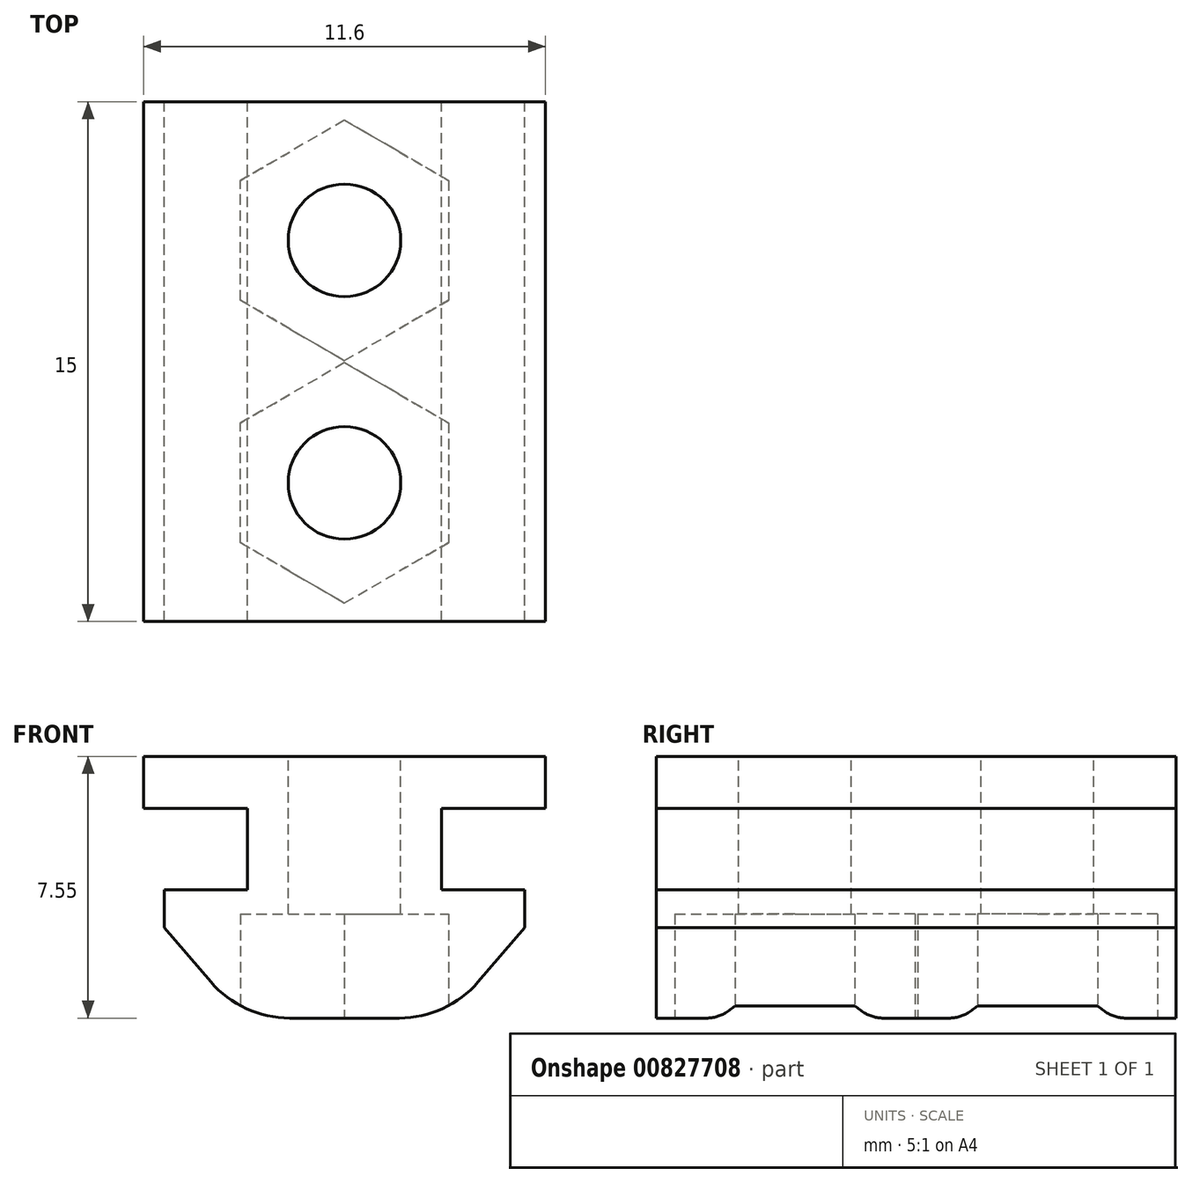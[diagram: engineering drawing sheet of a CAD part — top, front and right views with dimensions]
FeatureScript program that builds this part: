
annotation { "Feature Type Name" : "Feature", "Feature Type Description" : "" }
export const myFeature = defineFeature(function(context is Context, id is Id, definition is map)
    precondition{}
    {
        {
            var Q0;
            Q0=qCreatedBy(makeId("Front.planeOp"),FACE);
            var sketch = newSketch(context, id + "F0", { "sketchPlane" : qUnion([Q0])});
            skPoint(sketch, "E0.middle", {"position": v(0, 0) * mm});
            skLineSegment(sketch, "E1.0", {"start": v(2.8, 10) * mm, "end": v(2.8, 7.9) * mm});
            skLineSegment(sketch, "E1.1", {"start": v(2.8, 7.9) * mm, "end": v(5.2, 7.9) * mm});
            skLineSegment(sketch, "E1.2", {"start": v(5.2, 7.9) * mm, "end": v(5.2, 6.81) * mm});
            skLineSegment(sketch, "E1.3", {"start": v(5.2, 6.81) * mm, "end": v(2.96, 4.2) * mm});
            skLineSegment(sketch, "E1.4", {"start": v(2.96, 4.2) * mm, "end": v(0, 4.2) * mm});
            skLineSegment(sketch, "E1.5", {"start": v(-2.96, 4.2) * mm, "end": v(0, 4.2) * mm});
            skLineSegment(sketch, "E1.6", {"start": v(-2.8, 10) * mm, "end": v(-2.8, 7.9) * mm});
            skLineSegment(sketch, "E1.7", {"start": v(-2.8, 7.9) * mm, "end": v(-5.2, 7.9) * mm});
            skLineSegment(sketch, "E1.8", {"start": v(-5.2, 7.9) * mm, "end": v(-5.2, 6.81) * mm});
            skLineSegment(sketch, "E1.9", {"start": v(-5.2, 6.81) * mm, "end": v(-2.96, 4.2) * mm});
            skLineSegment(sketch, "E2", {"start": v(-2.8, 10) * mm, "end": v(-2.8, 10.25) * mm});
            skLineSegment(sketch, "E3", {"start": v(-2.8, 10.25) * mm, "end": v(-5.8, 10.25) * mm});
            skLineSegment(sketch, "E4", {"start": v(-5.8, 10.25) * mm, "end": v(-5.8, 11.75) * mm});
            skLineSegment(sketch, "E5", {"start": v(-5.8, 11.75) * mm, "end": v(0, 11.75) * mm});
            skLineSegment(sketch, "E6.MirrorCS", {"start": v(5.8, 11.75) * mm, "end": v(0, 11.75) * mm});
            skLineSegment(sketch, "E7.MirrorCS", {"start": v(5.8, 10.25) * mm, "end": v(5.8, 11.75) * mm});
            skLineSegment(sketch, "E8.MirrorCS", {"start": v(2.8, 10.25) * mm, "end": v(5.8, 10.25) * mm});
            skLineSegment(sketch, "E9.MirrorCS", {"start": v(2.8, 10) * mm, "end": v(2.8, 10.25) * mm});
            skSolve(sketch);
        }
        {
            var Q0;
            Q0=makeQuery(id+"F0.imprint","IMPRINT",FACE,{"disambiguationData":[TD([[makeQuery(id+"F0.imprint","IMPRINT",EDGE,{"derivedFrom":sQuery(id+"F0.wireOp",EDGE,"E1.0")}),-1.0]])]});
            extrude(context, id + "F1", {"entities" : qUnion([Q0]), "depth" : 15 * mm, "offsetDistance" : 25 * mm});
        }
        {
            var Q0;
            Q0=makeQuery(id+"F1.opExtrude","SWEPT_EDGE",EDGE,{"disambiguationData":[OSD([sQuery(id+"F0.wireOp",EDGE,"E1.5"),sQuery(id+"F0.wireOp",EDGE,"E1.9")])]});
            var Q1;
            Q1=makeQuery(id+"F1.opExtrude","SWEPT_EDGE",EDGE,{"disambiguationData":[OSD([sQuery(id+"F0.wireOp",EDGE,"E1.3"),sQuery(id+"F0.wireOp",EDGE,"E1.4")])]});
            fillet(context, id + "F2", {"entities" : qUnion([Q0, Q1]), "radius" : 3 * mm, "tangentPropagation" : true, "allowEdgeOverflow" : false});
        }
        {
            var Q0;
            Q0=makeQuery(id+"F1.opExtrude","SWEPT_FACE",FACE,{"disambiguationData":[OSD([sQuery(id+"F0.wireOp",EDGE,"E5"),sQuery(id+"F0.wireOp",EDGE,"E6.MirrorCS")])]});
            var sketch = newSketch(context, id + "F3", { "sketchPlane" : qUnion([Q0])});
            skCircle(sketch, "E10", {"center": v(0, -4) * mm, "radius": 1.63 * mm});
            skCircle(sketch, "E11", {"center": v(0, -11) * mm, "radius": 1.63 * mm});
            skSolve(sketch);
        }
        {
            var Q0;
            Q0=makeQuery(id+"F3.imprint","IMPRINT",FACE,{"disambiguationData":[TD([[makeQuery(id+"F3.imprint","IMPRINT",EDGE,{"derivedFrom":sQuery(id+"F3.wireOp",EDGE,"E10")}),1.0]])]});
            var Q1;
            Q1=makeQuery(id+"F3.imprint","IMPRINT",FACE,{"disambiguationData":[TD([[makeQuery(id+"F3.imprint","IMPRINT",EDGE,{"derivedFrom":sQuery(id+"F3.wireOp",EDGE,"E11")}),1.0]])]});
            extrude(context, id + "F4", {"entities" : qUnion([Q0, Q1]), "operationType" : NewBodyOperationType.REMOVE, "oppositeDirection" : true, "depth" : 6 * mm, "offsetDistance" : 25 * mm});
        }
        {
            var Q0;
            Q0=makeQuery(id+"F1.opExtrude","SWEPT_FACE",FACE,{"disambiguationData":[OSD([sQuery(id+"F0.wireOp",EDGE,"E1.4"),sQuery(id+"F0.wireOp",EDGE,"E1.5")])]});
            var sketch = newSketch(context, id + "F5", { "sketchPlane" : qUnion([Q0])});
            skCircle(sketch, "E12.0", {"center": v(0, 11) * mm, "radius": 1.63 * mm, "construction": true});
            skCircle(sketch, "E12.1", {"center": v(0, 4) * mm, "radius": 1.63 * mm, "construction": true});
            skLineSegment(sketch, "E13.0", {"start": v(0, 14.46) * mm, "end": v(3, 12.73) * mm});
            skLineSegment(sketch, "E13.1", {"start": v(3, 12.73) * mm, "end": v(3, 9.27) * mm});
            skLineSegment(sketch, "E13.2", {"start": v(3, 9.27) * mm, "end": v(0, 7.54) * mm});
            skLineSegment(sketch, "E13.3", {"start": v(0, 7.54) * mm, "end": v(-3, 9.27) * mm});
            skLineSegment(sketch, "E13.4", {"start": v(-3, 9.27) * mm, "end": v(-3, 12.73) * mm});
            skLineSegment(sketch, "E13.5", {"start": v(-3, 12.73) * mm, "end": v(0, 14.46) * mm});
            skPoint(sketch, "E13.0.midPoint", {"position": v(0, 14) * mm});
            skLineSegment(sketch, "E14.0", {"start": v(0, 7.46) * mm, "end": v(3, 5.73) * mm});
            skLineSegment(sketch, "E14.1", {"start": v(3, 5.73) * mm, "end": v(3, 2.27) * mm});
            skLineSegment(sketch, "E14.2", {"start": v(3, 2.27) * mm, "end": v(0, 0.54) * mm});
            skLineSegment(sketch, "E14.3", {"start": v(0, 0.54) * mm, "end": v(-3, 2.27) * mm});
            skLineSegment(sketch, "E14.4", {"start": v(-3, 2.27) * mm, "end": v(-3, 5.73) * mm});
            skLineSegment(sketch, "E14.5", {"start": v(-3, 5.73) * mm, "end": v(0, 7.46) * mm});
            skPoint(sketch, "E14.0.midPoint", {"position": v(0, 7) * mm});
            skSolve(sketch);
        }
        {
            var Q0;
            {var subQ0=sQuery(id+"F5.wireOp",EDGE,"E13.0");var subQ1=sQuery(id+"F0.wireOp",EDGE,"E1.5");var subQ2=sQuery(id+"F0.wireOp",EDGE,"E1.4");var subQ3=makeQuery(id+"F1.opExtrude","SWEPT_FACE",FACE,{"disambiguationData":[OSD([subQ2,subQ1])]});var subQ4=makeQuery(id+"F2.opFillet","BLEND_EDGE",EDGE,{"blendedFrom":[makeQuery(id+"F1.opExtrude","SWEPT_EDGE",EDGE,{"disambiguationData":[OSD([subQ1,sQuery(id+"F0.wireOp",EDGE,"E1.9")])]}),subQ3],"blendedInto":[subQ3]});var subQ5=makeQuery(id+"F5.imprint","INTERSECT",VERTEX,{"derivedFrom":[subQ4,subQ0]});Q0=makeQuery(id+"F5.imprint","IMPRINT",FACE,{"disambiguationData":[TD([[makeQuery(id+"F5.imprint","IMPRINT",EDGE,{"disambiguationData":[TD([[subQ5,-1.0]])],"derivedFrom":subQ0}),-1.0]])]});}
            var Q1;
            {var subQ5=sQuery(id+"F5.wireOp",EDGE,"E13.1");Q1=makeQuery(id+"F5.imprint","IMPRINT",FACE,{"disambiguationData":[TD([[makeQuery(id+"F5.imprint","IMPRINT",EDGE,{"derivedFrom":subQ5}),-1.0]])]});}
            var Q2;
            {var subQ1=sQuery(id+"F5.wireOp",EDGE,"E13.4");Q2=makeQuery(id+"F5.imprint","IMPRINT",FACE,{"disambiguationData":[TD([[makeQuery(id+"F5.imprint","IMPRINT",EDGE,{"derivedFrom":subQ1}),-1.0]])]});}
            var Q3;
            {var subQ0=sQuery(id+"F5.wireOp",EDGE,"E14.0");var subQ1=sQuery(id+"F0.wireOp",EDGE,"E1.5");var subQ2=sQuery(id+"F0.wireOp",EDGE,"E1.4");var subQ3=makeQuery(id+"F1.opExtrude","SWEPT_FACE",FACE,{"disambiguationData":[OSD([subQ2,subQ1])]});var subQ4=makeQuery(id+"F2.opFillet","BLEND_EDGE",EDGE,{"blendedFrom":[makeQuery(id+"F1.opExtrude","SWEPT_EDGE",EDGE,{"disambiguationData":[OSD([subQ1,sQuery(id+"F0.wireOp",EDGE,"E1.9")])]}),subQ3],"blendedInto":[subQ3]});var subQ5=makeQuery(id+"F5.imprint","INTERSECT",VERTEX,{"derivedFrom":[subQ4,subQ0]});Q3=makeQuery(id+"F5.imprint","IMPRINT",FACE,{"disambiguationData":[TD([[makeQuery(id+"F5.imprint","IMPRINT",EDGE,{"disambiguationData":[TD([[subQ5,-1.0]])],"derivedFrom":subQ0}),-1.0]])]});}
            var Q4;
            {var subQ1=sQuery(id+"F5.wireOp",EDGE,"E14.4");Q4=makeQuery(id+"F5.imprint","IMPRINT",FACE,{"disambiguationData":[TD([[makeQuery(id+"F5.imprint","IMPRINT",EDGE,{"derivedFrom":subQ1}),-1.0]])]});}
            var Q5;
            {var subQ5=sQuery(id+"F5.wireOp",EDGE,"E14.1");Q5=makeQuery(id+"F5.imprint","IMPRINT",FACE,{"disambiguationData":[TD([[makeQuery(id+"F5.imprint","IMPRINT",EDGE,{"derivedFrom":subQ5}),-1.0]])]});}
            var Q6;
            {var subQ0=sQuery(id+"F5.wireOp",EDGE,"E13.5");var subQ1=sQuery(id+"F5.wireOp",EDGE,"E13.0");var subQ2=makeQuery(id+"F5.imprint","INTERSECT",VERTEX,{"derivedFrom":[subQ1,subQ0]});Q6=makeQuery(id+"F5.imprint","IMPRINT",FACE,{"disambiguationData":[TD([[makeQuery(id+"F5.imprint","IMPRINT",EDGE,{"disambiguationData":[TD([[subQ2,-1.0]])],"derivedFrom":subQ1}),-1.0]])]});}
            var Q7;
            {var subQ0=sQuery(id+"F5.wireOp",EDGE,"E14.5");var subQ1=sQuery(id+"F5.wireOp",EDGE,"E14.0");var subQ2=makeQuery(id+"F5.imprint","INTERSECT",VERTEX,{"derivedFrom":[subQ1,subQ0]});Q7=makeQuery(id+"F5.imprint","IMPRINT",FACE,{"disambiguationData":[TD([[makeQuery(id+"F5.imprint","IMPRINT",EDGE,{"disambiguationData":[TD([[subQ2,-1.0]])],"derivedFrom":subQ1}),-1.0]])]});}
            extrude(context, id + "F6", {"entities" : qUnion([Q0, Q1, Q2, Q3, Q4, Q5, Q6, Q7]), "operationType" : NewBodyOperationType.REMOVE, "oppositeDirection" : true, "depth" : 3 * mm, "offsetDistance" : 25 * mm});
        }
    });
